# Revit family: Accessory-Teknion-ZNEL-Ledge_Table_Electric-R2019
name_source: partatom
category: Furniture
units: mm (PartAtom-declared; Revit-internal decimal feet)

## family parameters
Always vertical = Yes
Cut with Voids When Loaded = No
OmniClass Number = 23.40.20.00
OmniClass Title = General Furniture and Specialties
Room Calculation Point = No
Shared = Yes
Work Plane-Based = No

## types (4) — shared parameters
Assembly Code = E2020200
Height = 41 "
Manufacturer = Teknion
Manufacturer Fax = 416.661.4586
Part Number = ZNEL
Product Documentation Link = https://www.teknion.com
Product Line = Zones
Product Page URL = https://www.teknion.com
Series = Zones
Sustainability Data = https://www.teknion.com
URL = www.teknion.com
Unit Weight URL = http://www.teknion.com
Warranty = http://www.teknion.com

## per-type parameters (varying)
| type | Description | Model | Segment 2 Power 1 | Segment 2 Power 2 | Segment 3 Power 1 | Segment 3 Power 2 | Three Segment | Two Segment |
| Table Segment 2, Power 1 | Ledge Table Electric, Two Table Segments, Two AC Outlets. | ZNEL2__1 | Yes | No | No | No | No | Yes |
| Table Segment 2, Power 2 | Ledge Table Electric, Two Table Segments, AC and USB Outlets. | ZNEL2__2 | No | Yes | No | No | No | Yes |
| Table Segment 3, Power 1 | Ledge Table Electric, Three Table Segments, Two AC Outlets. | ZNEL3__1 | Yes | No | Yes | No | Yes | No |
| Table Segment 3, Power 2 | Ledge Table Electric, Three Table Segments, AC and USB Outlets. | ZNEL3__2 | No | Yes | No | Yes | Yes | No |

## geometry (parser evidence)
native form markers: Sweep x3
no freeform markers — native parametric forms only
